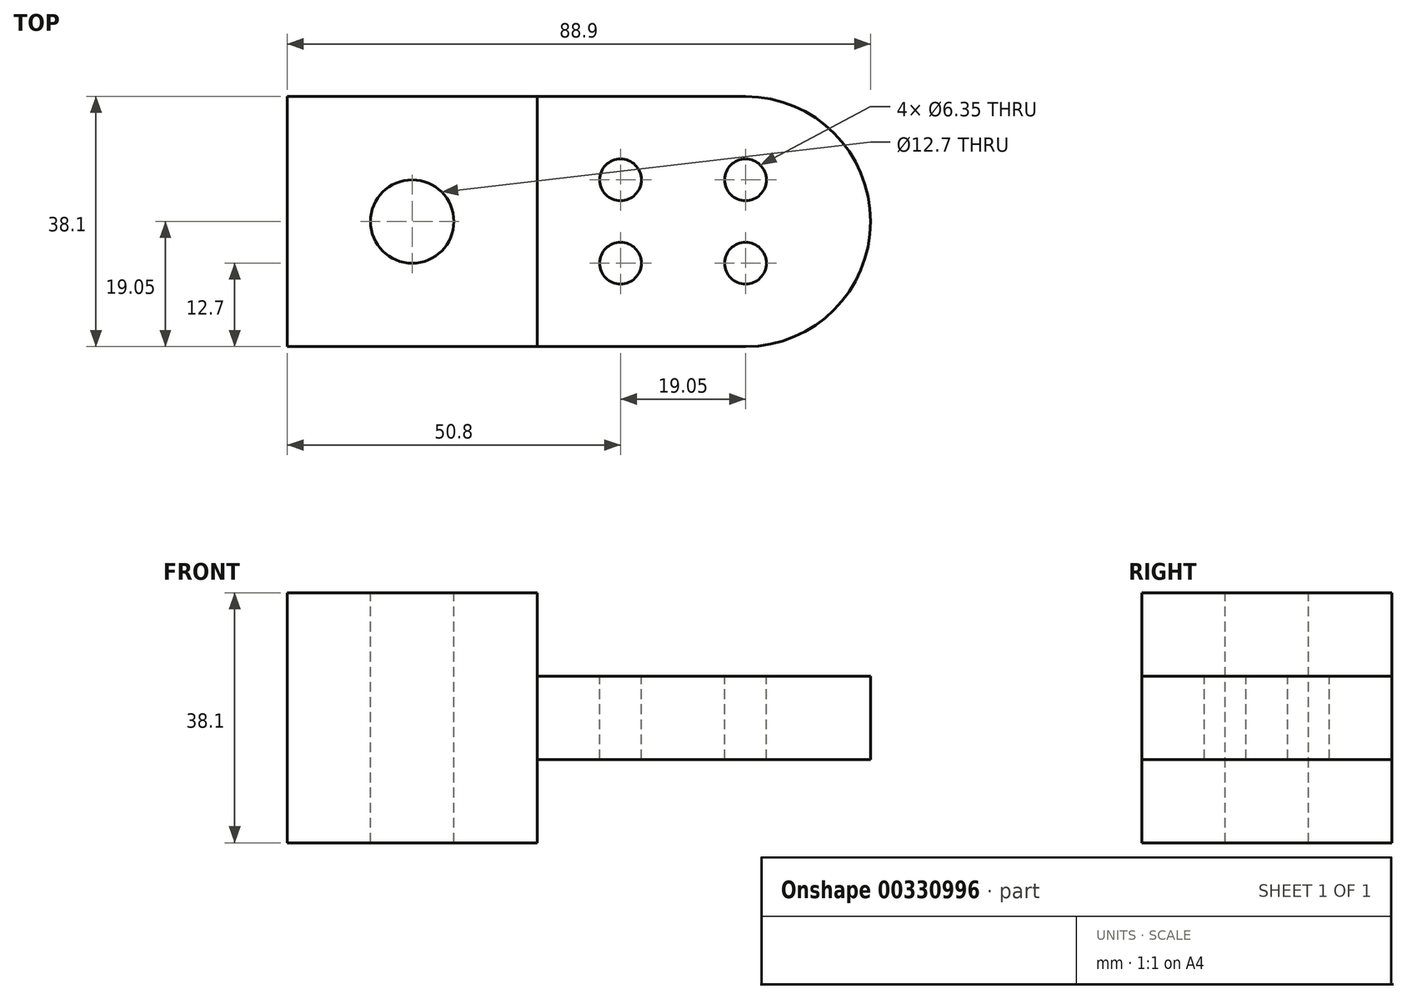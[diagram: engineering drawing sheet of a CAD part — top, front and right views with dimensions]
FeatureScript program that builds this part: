
annotation { "Feature Type Name" : "Feature", "Feature Type Description" : "" }
export const myFeature = defineFeature(function(context is Context, id is Id, definition is map)
    precondition{}
    {
        {
            var Q0;
            Q0=qCreatedBy(makeId("Top.planeOp"),FACE);
            var sketch = newSketch(context, id + "F0", { "sketchPlane" : qUnion([Q0])});
            skLineSegment(sketch, "E0", {"start": v(0, 0) * mm, "end": v(38.1, 0) * mm});
            skLineSegment(sketch, "E1", {"start": v(38.1, 0) * mm, "end": v(38.1, -38.1) * mm});
            skLineSegment(sketch, "E2", {"start": v(38.1, -38.1) * mm, "end": v(0, -38.1) * mm});
            skLineSegment(sketch, "E3", {"start": v(0, -38.1) * mm, "end": v(0, 0) * mm});
            skSolve(sketch);
        }
        {
            var Q0;
            Q0 = qSketchRegion(id + "F0", true);
            extrude(context, id + "F1", {"entities" : qUnion([Q0]), "endBound" : BoundingType.SYMMETRIC, "depth" : 38.1 * mm});
        }
        {
            var Q0;
            Q0=qCreatedBy(makeId("Top.planeOp"),FACE);
            var sketch = newSketch(context, id + "F2", { "sketchPlane" : qUnion([Q0])});
            skLineSegment(sketch, "E4", {"start": v(0, 0) * mm, "end": v(38.1, 0) * mm});
            skLineSegment(sketch, "E5", {"start": v(38.1, 0) * mm, "end": v(69.85, 0) * mm});
            skLineSegment(sketch, "E6", {"start": v(38.1, 0) * mm, "end": v(38.1, -38.1) * mm});
            skLineSegment(sketch, "E7", {"start": v(38.1, -38.1) * mm, "end": v(69.85, -38.1) * mm});
            skArc(sketch, "E8", {"start": v(69.85, -38.1) * mm, "mid": v(88.9, -19.05) * mm, "end": v(69.85, 0) * mm});
            skSolve(sketch);
        }
        {
            var Q0;
            Q0 = qSketchRegion(id + "F2", true);
            extrude(context, id + "F3", {"entities" : qUnion([Q0]), "operationType" : NewBodyOperationType.ADD, "endBound" : BoundingType.SYMMETRIC, "oppositeDirection" : true, "depth" : 12.7 * mm});
        }
        {
            var Q0;
            Q0=makeQuery(id+"F1.opExtrude","CAP_FACE",FACE,{"disambiguationData":[OSD([sQuery(id+"F0.wireOp",EDGE,"E0"),sQuery(id+"F0.wireOp",EDGE,"E1"),sQuery(id+"F0.wireOp",EDGE,"E2"),sQuery(id+"F0.wireOp",EDGE,"E3")])],"isStart":false});
            var sketch = newSketch(context, id + "F4", { "sketchPlane" : qUnion([Q0])});
            skCircle(sketch, "E9", {"center": v(19.05, -19.05) * mm, "radius": 6.35 * mm});
            skSolve(sketch);
        }
        {
            var Q0;
            Q0 = qSketchRegion(id + "F4", true);
            extrude(context, id + "F5", {"entities" : qUnion([Q0]), "operationType" : NewBodyOperationType.REMOVE, "oppositeDirection" : true, "depth" : 74.17 * mm});
        }
        {
            var Q0;
            Q0=makeQuery(id+"F3.opExtrude","CAP_FACE",FACE,{"disambiguationData":[OSD([sQuery(id+"F2.wireOp",EDGE,"E5"),sQuery(id+"F2.wireOp",EDGE,"E6"),sQuery(id+"F2.wireOp",EDGE,"E7"),sQuery(id+"F2.wireOp",EDGE,"E8")])],"isStart":true});
            var sketch = newSketch(context, id + "F6", { "sketchPlane" : qUnion([Q0])});
            skLineSegment(sketch, "E10.bottom", {"start": v(38.1, 0) * mm, "end": v(50.8, 0) * mm, "construction": true});
            skLineSegment(sketch, "E10.top", {"start": v(38.1, -12.7) * mm, "end": v(50.8, -12.7) * mm, "construction": true});
            skLineSegment(sketch, "E10.left", {"start": v(38.1, 0) * mm, "end": v(38.1, -12.7) * mm, "construction": true});
            skLineSegment(sketch, "E10.right", {"start": v(50.8, 0) * mm, "end": v(50.8, -12.7) * mm, "construction": true});
            skCircle(sketch, "E11", {"center": v(50.8, -12.7) * mm, "radius": 3.18 * mm});
            skLineSegment(sketch, "E12.bottom", {"start": v(38.1, -38.1) * mm, "end": v(50.8, -38.1) * mm, "construction": true});
            skLineSegment(sketch, "E12.top", {"start": v(38.1, -25.4) * mm, "end": v(50.8, -25.4) * mm, "construction": true});
            skLineSegment(sketch, "E12.left", {"start": v(38.1, -38.1) * mm, "end": v(38.1, -25.4) * mm, "construction": true});
            skLineSegment(sketch, "E12.right", {"start": v(50.8, -38.1) * mm, "end": v(50.8, -25.4) * mm, "construction": true});
            skCircle(sketch, "E13", {"center": v(50.8, -25.4) * mm, "radius": 3.18 * mm});
            skLineSegment(sketch, "E14.bottom", {"start": v(69.85, 0) * mm, "end": v(57.15, 0) * mm, "construction": true});
            skLineSegment(sketch, "E14.top", {"start": v(69.85, -12.7) * mm, "end": v(57.15, -12.7) * mm, "construction": true});
            skLineSegment(sketch, "E14.left", {"start": v(69.85, 0) * mm, "end": v(69.85, -12.7) * mm, "construction": true});
            skLineSegment(sketch, "E14.right", {"start": v(57.15, 0) * mm, "end": v(57.15, -12.7) * mm, "construction": true});
            skLineSegment(sketch, "E15.bottom", {"start": v(69.85, -38.1) * mm, "end": v(57.15, -38.1) * mm, "construction": true});
            skLineSegment(sketch, "E15.top", {"start": v(69.85, -25.4) * mm, "end": v(57.15, -25.4) * mm, "construction": true});
            skLineSegment(sketch, "E15.left", {"start": v(69.85, -38.1) * mm, "end": v(69.85, -25.4) * mm, "construction": true});
            skLineSegment(sketch, "E15.right", {"start": v(57.15, -38.1) * mm, "end": v(57.15, -25.4) * mm, "construction": true});
            skCircle(sketch, "E16", {"center": v(69.85, -12.7) * mm, "radius": 3.18 * mm});
            skCircle(sketch, "E17", {"center": v(69.85, -25.4) * mm, "radius": 3.18 * mm});
            skSolve(sketch);
        }
        {
            var Q0;
            Q0=makeQuery(id+"F6.imprint","IMPRINT",FACE,{"disambiguationData":[TD([[makeQuery(id+"F6.imprint","IMPRINT",EDGE,{"derivedFrom":sQuery(id+"F6.wireOp",EDGE,"E13")}),1.0]])]});
            var Q1;
            Q1=makeQuery(id+"F6.imprint","IMPRINT",FACE,{"disambiguationData":[TD([[makeQuery(id+"F6.imprint","IMPRINT",EDGE,{"derivedFrom":sQuery(id+"F6.wireOp",EDGE,"E16")}),1.0]])]});
            var Q2;
            Q2=makeQuery(id+"F6.imprint","IMPRINT",FACE,{"disambiguationData":[TD([[makeQuery(id+"F6.imprint","IMPRINT",EDGE,{"derivedFrom":sQuery(id+"F6.wireOp",EDGE,"E17")}),1.0]])]});
            var Q3;
            Q3=makeQuery(id+"F6.imprint","IMPRINT",FACE,{"disambiguationData":[TD([[makeQuery(id+"F6.imprint","IMPRINT",EDGE,{"derivedFrom":sQuery(id+"F6.wireOp",EDGE,"E11")}),1.0]])]});
            extrude(context, id + "F7", {"entities" : qUnion([Q0, Q1, Q2, Q3]), "operationType" : NewBodyOperationType.REMOVE, "oppositeDirection" : true, "depth" : 25.4 * mm});
        }
    });
